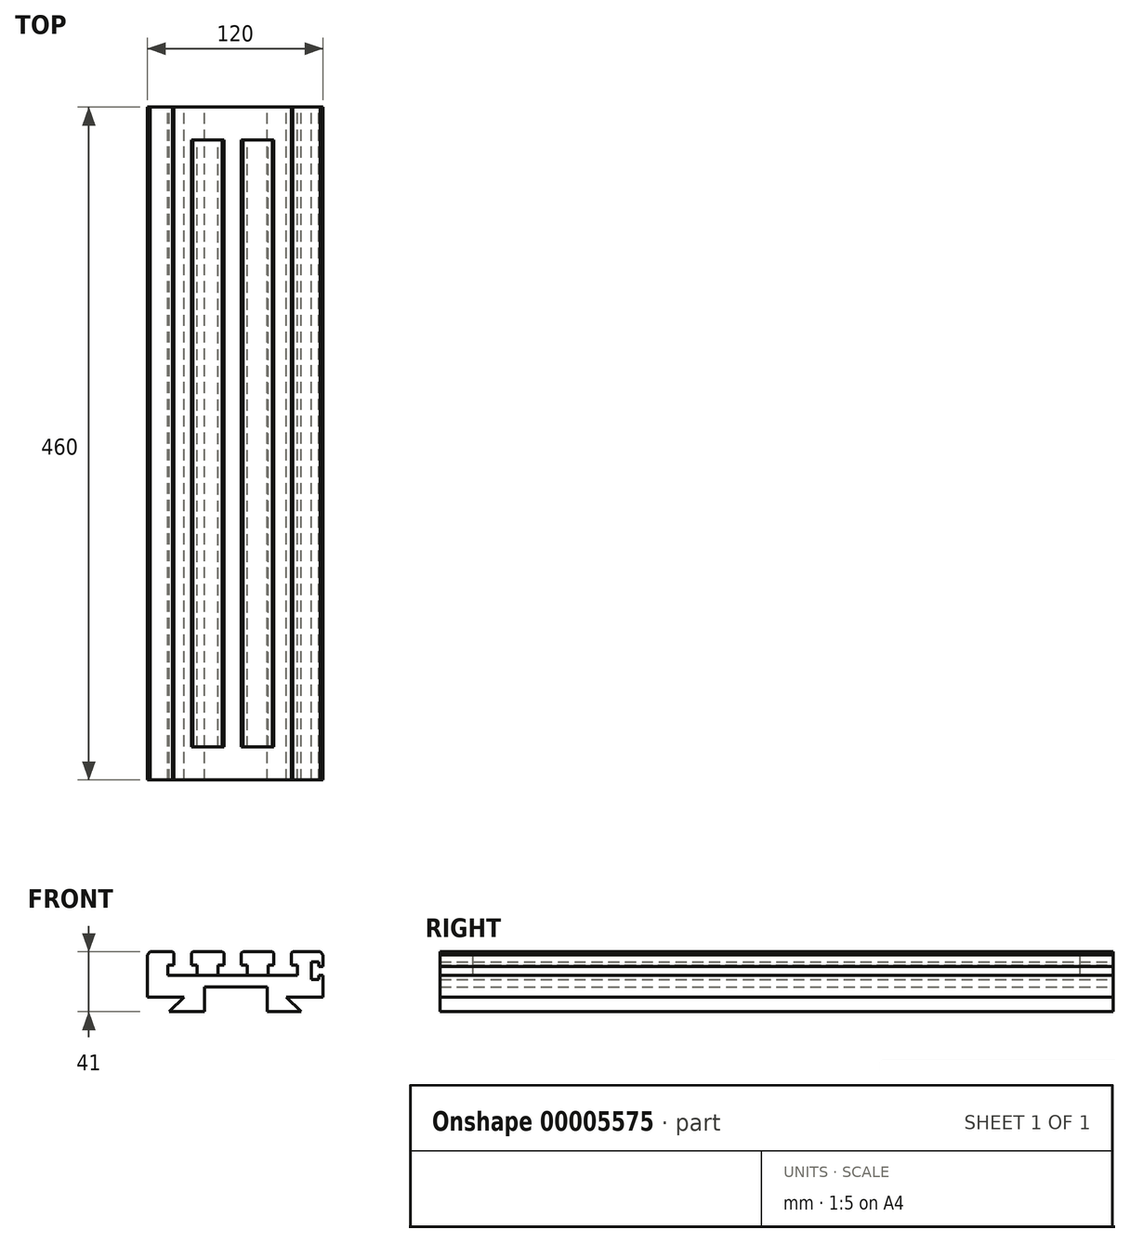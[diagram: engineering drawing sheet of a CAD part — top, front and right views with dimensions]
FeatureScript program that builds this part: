
annotation { "Feature Type Name" : "Feature", "Feature Type Description" : "" }
export const myFeature = defineFeature(function(context is Context, id is Id, definition is map)
    precondition{}
    {
        {
            var Q0;
            Q0=qCreatedBy(makeId("Front.planeOp"),FACE);
            var sketch = newSketch(context, id + "F0", { "sketchPlane" : qUnion([Q0])});
            skLineSegment(sketch, "E0", {"start": v(-69.68, 16) * mm, "end": v(-51.68, 16) * mm});
            skLineSegment(sketch, "E1", {"start": v(-51.68, 16) * mm, "end": v(-51.68, 7) * mm});
            skLineSegment(sketch, "E2", {"start": v(-51.68, 7) * mm, "end": v(-55.68, 7) * mm});
            skLineSegment(sketch, "E3", {"start": v(-55.68, 7) * mm, "end": v(-55.68, 0) * mm});
            skLineSegment(sketch, "E4", {"start": v(-55.68, 0) * mm, "end": v(-35.68, 0) * mm});
            skLineSegment(sketch, "E5", {"start": v(-35.68, 0) * mm, "end": v(-35.68, 7) * mm});
            skLineSegment(sketch, "E6", {"start": v(-35.68, 7) * mm, "end": v(-39.68, 7) * mm});
            skLineSegment(sketch, "E7", {"start": v(-39.68, 7) * mm, "end": v(-39.68, 16) * mm});
            skLineSegment(sketch, "E8", {"start": v(-39.68, 16) * mm, "end": v(-17.43, 16) * mm});
            skLineSegment(sketch, "E9", {"start": v(-17.43, 16) * mm, "end": v(-17.43, 7) * mm});
            skLineSegment(sketch, "E10", {"start": v(-17.43, 7) * mm, "end": v(-21.43, 7) * mm});
            skLineSegment(sketch, "E11", {"start": v(-21.43, 7) * mm, "end": v(-21.43, 0) * mm});
            skLineSegment(sketch, "E12", {"start": v(-21.43, 0) * mm, "end": v(-1.43, 0) * mm});
            skLineSegment(sketch, "E13", {"start": v(-1.43, 0) * mm, "end": v(-1.43, 7) * mm});
            skLineSegment(sketch, "E14", {"start": v(-1.43, 7) * mm, "end": v(-5.43, 7) * mm});
            skLineSegment(sketch, "E15", {"start": v(-5.43, 7) * mm, "end": v(-5.43, 16) * mm});
            skLineSegment(sketch, "E16", {"start": v(-5.43, 16) * mm, "end": v(16.82, 16) * mm});
            skLineSegment(sketch, "E17", {"start": v(16.82, 16) * mm, "end": v(16.82, 7) * mm});
            skLineSegment(sketch, "E18", {"start": v(16.82, 7) * mm, "end": v(12.82, 7) * mm});
            skLineSegment(sketch, "E19", {"start": v(12.82, 7) * mm, "end": v(12.82, 0) * mm});
            skLineSegment(sketch, "E20", {"start": v(12.82, 0) * mm, "end": v(32.82, 0) * mm});
            skLineSegment(sketch, "E21", {"start": v(32.82, 0) * mm, "end": v(32.82, 7) * mm});
            skLineSegment(sketch, "E22", {"start": v(32.82, 7) * mm, "end": v(28.82, 7) * mm});
            skLineSegment(sketch, "E23", {"start": v(28.82, 7) * mm, "end": v(28.82, 16) * mm});
            skLineSegment(sketch, "E24", {"start": v(28.82, 16) * mm, "end": v(50.32, 16) * mm});
            skLineSegment(sketch, "E25", {"start": v(35.32, -25) * mm, "end": v(12.32, -25) * mm});
            skLineSegment(sketch, "E26", {"start": v(12.32, -25) * mm, "end": v(12.32, -8) * mm});
            skLineSegment(sketch, "E27", {"start": v(12.32, -8) * mm, "end": v(-30.68, -8) * mm});
            skLineSegment(sketch, "E28", {"start": v(-30.68, -8) * mm, "end": v(-30.68, -25) * mm});
            skLineSegment(sketch, "E29", {"start": v(-69.68, 16) * mm, "end": v(-69.68, -15) * mm});
            skLineSegment(sketch, "E30", {"start": v(-51.68, 16) * mm, "end": v(-39.68, 16) * mm, "construction": true});
            skLineSegment(sketch, "E31", {"start": v(-17.43, 16) * mm, "end": v(-5.43, 16) * mm, "construction": true});
            skLineSegment(sketch, "E32", {"start": v(16.82, 16) * mm, "end": v(28.82, 16) * mm, "construction": true});
            skLineSegment(sketch, "E33", {"start": v(50.32, 16) * mm, "end": v(50.32, 6) * mm});
            skLineSegment(sketch, "E34", {"start": v(50.32, 6) * mm, "end": v(47.32, 6) * mm});
            skLineSegment(sketch, "E35", {"start": v(47.32, 6) * mm, "end": v(47.32, 9.03) * mm});
            skLineSegment(sketch, "E36", {"start": v(47.32, 9.03) * mm, "end": v(42.32, 9.03) * mm});
            skLineSegment(sketch, "E37", {"start": v(42.32, 9.03) * mm, "end": v(42.32, -2.97) * mm});
            skLineSegment(sketch, "E38", {"start": v(42.32, -2.97) * mm, "end": v(47.32, -2.97) * mm});
            skLineSegment(sketch, "E39", {"start": v(47.32, -2.97) * mm, "end": v(47.32, 0) * mm});
            skLineSegment(sketch, "E40", {"start": v(47.32, 0) * mm, "end": v(50.32, 0) * mm});
            skLineSegment(sketch, "E41", {"start": v(47.32, 16) * mm, "end": v(47.32, -25) * mm, "construction": true});
            skLineSegment(sketch, "E42", {"start": v(50.32, 0) * mm, "end": v(50.32, -15) * mm});
            skLineSegment(sketch, "E43", {"start": v(50.32, -15) * mm, "end": v(25.32, -15) * mm});
            skLineSegment(sketch, "E44", {"start": v(25.32, -15) * mm, "end": v(35.32, -25) * mm});
            skLineSegment(sketch, "E45", {"start": v(35.32, -25) * mm, "end": v(-75.78, -25) * mm, "construction": true});
            skLineSegment(sketch, "E46", {"start": v(-30.68, -25) * mm, "end": v(-54.68, -25) * mm});
            skLineSegment(sketch, "E47", {"start": v(-54.68, -25) * mm, "end": v(-44.68, -15) * mm});
            skLineSegment(sketch, "E48", {"start": v(-44.68, -15) * mm, "end": v(-69.68, -15) * mm});
            skLineSegment(sketch, "E49", {"start": v(50.32, -15) * mm, "end": v(-85.03, -15) * mm, "construction": true});
            skSolve(sketch);
        }
        {
            var Q0;
            Q0=makeQuery(id+"F0.imprint","IMPRINT",FACE,{"disambiguationData":[TD([[makeQuery(id+"F0.imprint","IMPRINT",EDGE,{"derivedFrom":sQuery(id+"F0.wireOp",EDGE,"E0")}),-1.0]])]});
            extrude(context, id + "F1", {"entities" : qUnion([Q0]), "depth" : 460 * mm});
        }
        {
            var Q0;
            Q0=makeQuery(id+"F1.opExtrude","SWEPT_FACE",FACE,{"disambiguationData":[OSD([sQuery(id+"F0.wireOp",EDGE,"E1")])]});
            var sketch = newSketch(context, id + "F2", { "sketchPlane" : qUnion([Q0])});
            skLineSegment(sketch, "E50.bottom", {"start": v(0, 16) * mm, "end": v(-22.5, 16) * mm});
            skLineSegment(sketch, "E50.top", {"start": v(0, 0) * mm, "end": v(-22.5, 0) * mm});
            skLineSegment(sketch, "E50.left", {"start": v(0, 16) * mm, "end": v(0, 0) * mm});
            skLineSegment(sketch, "E50.right", {"start": v(-22.5, 16) * mm, "end": v(-22.5, 0) * mm});
            skLineSegment(sketch, "E51.bottom", {"start": v(-460, 16) * mm, "end": v(-437.5, 16) * mm});
            skLineSegment(sketch, "E51.top", {"start": v(-460, 0) * mm, "end": v(-437.5, 0) * mm});
            skLineSegment(sketch, "E51.left", {"start": v(-460, 16) * mm, "end": v(-460, 0) * mm});
            skLineSegment(sketch, "E51.right", {"start": v(-437.5, 16) * mm, "end": v(-437.5, 0) * mm});
            skSolve(sketch);
        }
        {
            var Q0;
            {var subQ7=sQuery(id+"F2.wireOp",EDGE,"E50.top");var subQ13=sQuery(id+"F2.wireOp",EDGE,"E51.top");var subQ15=sQuery(id+"F2.wireOp",EDGE,"E50.bottom");var subQ16=sQuery(id+"F2.wireOp",EDGE,"E51.bottom");Q0=qUnion([makeQuery(id+"F2.imprint","IMPRINT",FACE,{"disambiguationData":[TD([[makeQuery(id+"F2.imprint","IMPRINT",EDGE,{"derivedFrom":subQ7}),-1.0]])]}),makeQuery(id+"F2.imprint","IMPRINT",FACE,{"disambiguationData":[TD([[makeQuery(id+"F2.imprint","IMPRINT",EDGE,{"derivedFrom":subQ13}),1.0]])]}),makeQuery(id+"F2.imprint","IMPRINT",FACE,{"disambiguationData":[TD([[makeQuery(id+"F2.imprint","IMPRINT",EDGE,{"derivedFrom":subQ15}),-1.0]])]}),makeQuery(id+"F2.imprint","IMPRINT",FACE,{"disambiguationData":[TD([[makeQuery(id+"F2.imprint","IMPRINT",EDGE,{"derivedFrom":subQ16}),-1.0]])]})]);}
            extrude(context, id + "F3", {"entities" : qUnion([Q0]), "operationType" : NewBodyOperationType.REMOVE, "depth" : 80 * mm});
        }
        {
            var Q0;
            Q0=makeQuery(id+"F1.opExtrude","SWEPT_EDGE",EDGE,{"disambiguationData":[OSD([sQuery(id+"F0.wireOp",EDGE,"E0"),sQuery(id+"F0.wireOp",EDGE,"E1")])]});
            chamfer(context, id + "F4", {"entities" : qUnion([Q0]), "width" : 1 * mm, "tangentPropagation" : true});
        }
        {
            var Q0;
            Q0=makeQuery(id+"F1.opExtrude","SWEPT_EDGE",EDGE,{"disambiguationData":[OSD([sQuery(id+"F0.wireOp",EDGE,"E7"),sQuery(id+"F0.wireOp",EDGE,"E8")])]});
            var Q1;
            Q1=makeQuery(id+"F1.opExtrude","SWEPT_EDGE",EDGE,{"disambiguationData":[OSD([sQuery(id+"F0.wireOp",EDGE,"E8"),sQuery(id+"F0.wireOp",EDGE,"E9")])]});
            var Q2;
            Q2=makeQuery(id+"F1.opExtrude","SWEPT_EDGE",EDGE,{"disambiguationData":[OSD([sQuery(id+"F0.wireOp",EDGE,"E15"),sQuery(id+"F0.wireOp",EDGE,"E16")])]});
            var Q3;
            Q3=makeQuery(id+"F1.opExtrude","SWEPT_EDGE",EDGE,{"disambiguationData":[OSD([sQuery(id+"F0.wireOp",EDGE,"E16"),sQuery(id+"F0.wireOp",EDGE,"E17")])]});
            var Q4;
            Q4=makeQuery(id+"F1.opExtrude","SWEPT_EDGE",EDGE,{"disambiguationData":[OSD([sQuery(id+"F0.wireOp",EDGE,"E23"),sQuery(id+"F0.wireOp",EDGE,"E24")])]});
            chamfer(context, id + "F5", {"entities" : qUnion([Q0, Q1, Q2, Q3, Q4]), "width" : 1 * mm, "tangentPropagation" : true});
        }
        {
            var Q0;
            Q0=makeQuery(id+"F1.opExtrude","SWEPT_EDGE",EDGE,{"disambiguationData":[OSD([sQuery(id+"F0.wireOp",EDGE,"E24"),sQuery(id+"F0.wireOp",EDGE,"E33")])]});
            var Q1;
            Q1=makeQuery(id+"F1.opExtrude","SWEPT_EDGE",EDGE,{"disambiguationData":[OSD([sQuery(id+"F0.wireOp",EDGE,"E0"),sQuery(id+"F0.wireOp",EDGE,"E29")])]});
            chamfer(context, id + "F6", {"entities" : qUnion([Q0, Q1]), "width" : 2 * mm});
        }
    });
